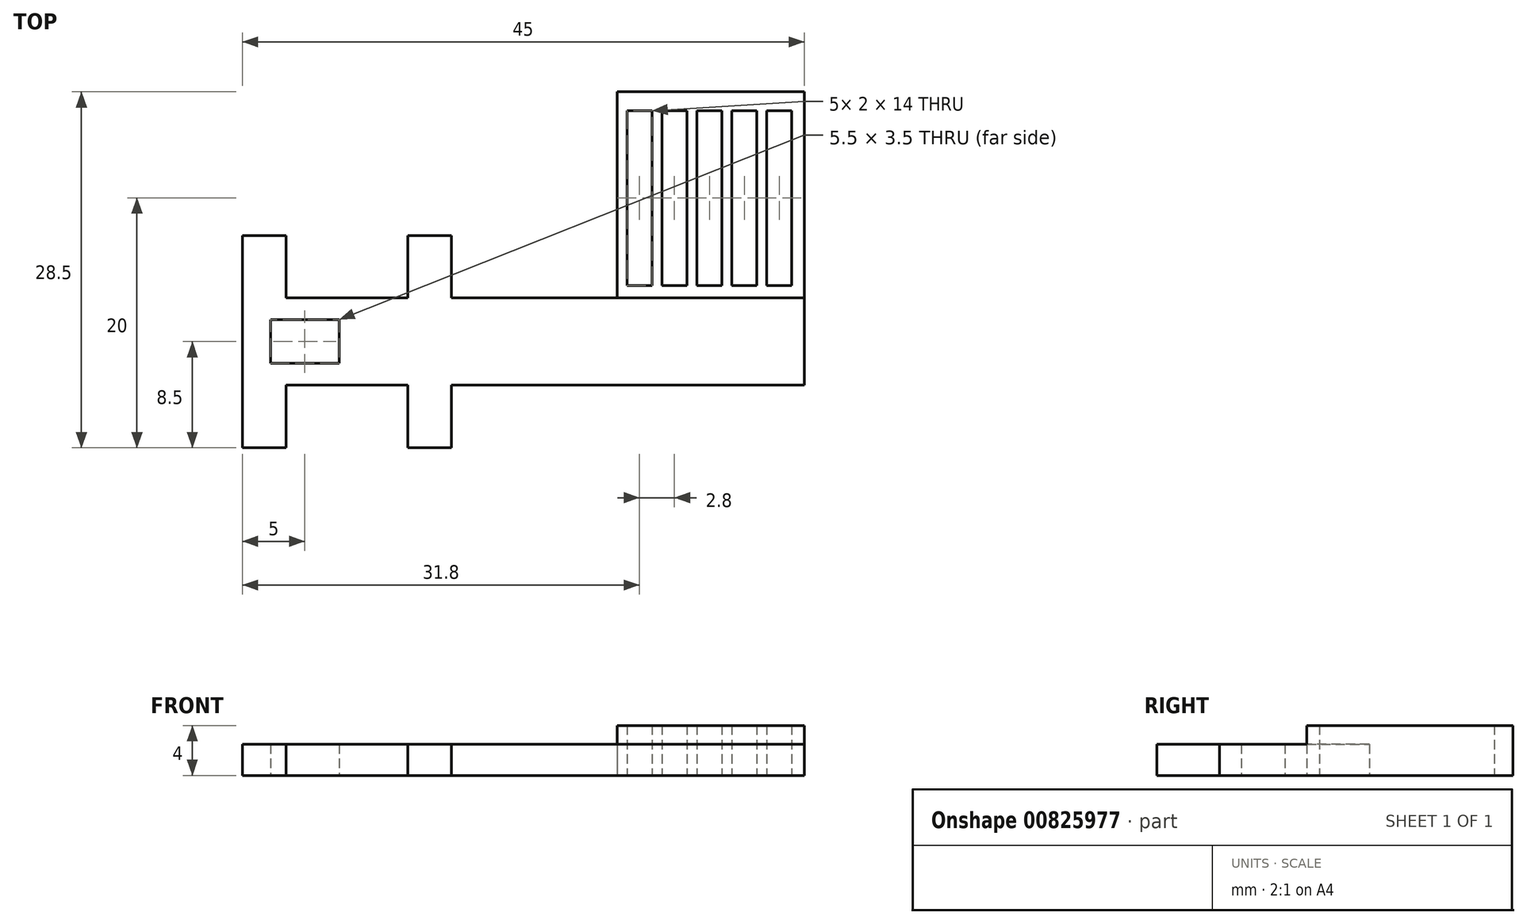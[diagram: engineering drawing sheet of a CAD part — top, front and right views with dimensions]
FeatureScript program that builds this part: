
annotation { "Feature Type Name" : "Feature", "Feature Type Description" : "" }
export const myFeature = defineFeature(function(context is Context, id is Id, definition is map)
    precondition{}
    {
        {
            var Q0;
            Q0=qCreatedBy(makeId("Top.planeOp"),FACE);
            var sketch = newSketch(context, id + "F0", { "sketchPlane" : qUnion([Q0])});
            skLineSegment(sketch, "E0.bottom", {"start": v(15, 3.5) * mm, "end": v(-15, 3.5) * mm});
            skLineSegment(sketch, "E0.top", {"start": v(15, -3.5) * mm, "end": v(-15, -3.5) * mm});
            skLineSegment(sketch, "E0.left", {"start": v(15, 3.5) * mm, "end": v(15, -3.5) * mm});
            skLineSegment(sketch, "E0.right", {"start": v(-15, 3.5) * mm, "end": v(-15, -3.5) * mm});
            skPoint(sketch, "E0.middle", {"position": v(0, 0) * mm});
            skLineSegment(sketch, "E1.bottom", {"start": v(-12.75, 1.75) * mm, "end": v(-7.25, 1.75) * mm});
            skLineSegment(sketch, "E1.top", {"start": v(-12.75, -1.75) * mm, "end": v(-7.25, -1.75) * mm});
            skLineSegment(sketch, "E1.left", {"start": v(-12.75, 1.75) * mm, "end": v(-12.75, -1.75) * mm});
            skLineSegment(sketch, "E1.right", {"start": v(-7.25, 1.75) * mm, "end": v(-7.25, -1.75) * mm});
            skPoint(sketch, "E1.middle", {"position": v(-10, 0) * mm});
            skLineSegment(sketch, "E2.bottom", {"start": v(1.75, 3.5) * mm, "end": v(-1.75, 3.5) * mm});
            skLineSegment(sketch, "E2.top", {"start": v(1.75, 8.5) * mm, "end": v(-1.75, 8.5) * mm});
            skLineSegment(sketch, "E2.left", {"start": v(1.75, 3.5) * mm, "end": v(1.75, 8.5) * mm});
            skLineSegment(sketch, "E2.right", {"start": v(-1.75, 3.5) * mm, "end": v(-1.75, 8.5) * mm});
            skPoint(sketch, "E2.middle", {"position": v(0, 6) * mm});
            skPoint(sketch, "E2.middle.positionSnap0", {"position": v(0, 3.5) * mm});
            skPoint(sketch, "E2.centerSnap0", {"position": v(0, 3.5) * mm});
            skLineSegment(sketch, "E3.bottom", {"start": v(1.75, -3.5) * mm, "end": v(-1.75, -3.5) * mm});
            skLineSegment(sketch, "E3.top", {"start": v(1.75, -8.5) * mm, "end": v(-1.75, -8.5) * mm});
            skLineSegment(sketch, "E3.left", {"start": v(1.75, -3.5) * mm, "end": v(1.75, -8.5) * mm});
            skLineSegment(sketch, "E3.right", {"start": v(-1.75, -3.5) * mm, "end": v(-1.75, -8.5) * mm});
            skPoint(sketch, "E3.middle", {"position": v(0, -6) * mm});
            skLineSegment(sketch, "E4.bottom", {"start": v(-15, 3.5) * mm, "end": v(-11.5, 3.5) * mm});
            skLineSegment(sketch, "E4.top", {"start": v(-15, 8.5) * mm, "end": v(-11.5, 8.5) * mm});
            skLineSegment(sketch, "E4.left", {"start": v(-15, 3.5) * mm, "end": v(-15, 8.5) * mm});
            skLineSegment(sketch, "E4.right", {"start": v(-11.5, 3.5) * mm, "end": v(-11.5, 8.5) * mm});
            skPoint(sketch, "E4.middle", {"position": v(-13.25, 6) * mm});
            skLineSegment(sketch, "E5.bottom", {"start": v(-15, -3.5) * mm, "end": v(-11.5, -3.5) * mm});
            skLineSegment(sketch, "E5.top", {"start": v(-15, -8.5) * mm, "end": v(-11.5, -8.5) * mm});
            skLineSegment(sketch, "E5.left", {"start": v(-15, -3.5) * mm, "end": v(-15, -8.5) * mm});
            skLineSegment(sketch, "E5.right", {"start": v(-11.5, -3.5) * mm, "end": v(-11.5, -8.5) * mm});
            skPoint(sketch, "E5.middle", {"position": v(-13.25, -6) * mm});
            skLineSegment(sketch, "E6.bottom", {"start": v(15, 3.5) * mm, "end": v(15, 3.5) * mm});
            skLineSegment(sketch, "E6.top", {"start": v(15, -3.5) * mm, "end": v(15, -3.5) * mm});
            skLineSegment(sketch, "E7.bottom", {"start": v(15, 3.5) * mm, "end": v(30, 3.5) * mm});
            skLineSegment(sketch, "E7.top", {"start": v(15, -3.5) * mm, "end": v(30, -3.5) * mm});
            skLineSegment(sketch, "E7.right", {"start": v(30, 3.5) * mm, "end": v(30, -3.5) * mm});
            skLineSegment(sketch, "E8.top", {"start": v(15, 20) * mm, "end": v(30, 20) * mm});
            skLineSegment(sketch, "E8.left", {"start": v(15, 3.5) * mm, "end": v(15, 20) * mm});
            skLineSegment(sketch, "E8.right", {"start": v(30, 3.5) * mm, "end": v(30, 20) * mm});
            skLineSegment(sketch, "E9.bottom", {"start": v(15.8, 18.5) * mm, "end": v(17.8, 18.5) * mm});
            skLineSegment(sketch, "E9.top", {"start": v(15.8, 4.5) * mm, "end": v(17.8, 4.5) * mm});
            skLineSegment(sketch, "E9.left", {"start": v(15.8, 18.5) * mm, "end": v(15.8, 4.5) * mm});
            skLineSegment(sketch, "E9.right", {"start": v(17.8, 18.5) * mm, "end": v(17.8, 4.5) * mm});
            skLineSegment(sketch, "E10.bottom", {"start": v(18.6, 18.5) * mm, "end": v(20.6, 18.5) * mm});
            skLineSegment(sketch, "E10.top", {"start": v(18.6, 4.5) * mm, "end": v(20.6, 4.5) * mm});
            skLineSegment(sketch, "E10.left", {"start": v(18.6, 18.5) * mm, "end": v(18.6, 4.5) * mm});
            skLineSegment(sketch, "E10.right", {"start": v(20.6, 18.5) * mm, "end": v(20.6, 4.5) * mm});
            skLineSegment(sketch, "E11.bottom", {"start": v(21.4, 18.5) * mm, "end": v(23.4, 18.5) * mm});
            skLineSegment(sketch, "E11.top", {"start": v(21.4, 4.5) * mm, "end": v(23.4, 4.5) * mm});
            skLineSegment(sketch, "E11.left", {"start": v(21.4, 18.5) * mm, "end": v(21.4, 4.5) * mm});
            skLineSegment(sketch, "E11.right", {"start": v(23.4, 18.5) * mm, "end": v(23.4, 4.5) * mm});
            skLineSegment(sketch, "E12.bottom", {"start": v(24.2, 18.5) * mm, "end": v(26.2, 18.5) * mm});
            skLineSegment(sketch, "E12.top", {"start": v(24.2, 4.5) * mm, "end": v(26.2, 4.5) * mm});
            skLineSegment(sketch, "E12.left", {"start": v(24.2, 18.5) * mm, "end": v(24.2, 4.5) * mm});
            skLineSegment(sketch, "E12.right", {"start": v(26.2, 18.5) * mm, "end": v(26.2, 4.5) * mm});
            skLineSegment(sketch, "E13.bottom", {"start": v(27, 18.5) * mm, "end": v(29, 18.5) * mm});
            skLineSegment(sketch, "E13.top", {"start": v(27, 4.5) * mm, "end": v(29, 4.5) * mm});
            skLineSegment(sketch, "E13.left", {"start": v(27, 18.5) * mm, "end": v(27, 4.5) * mm});
            skLineSegment(sketch, "E13.right", {"start": v(29, 18.5) * mm, "end": v(29, 4.5) * mm});
            skSolve(sketch);
        }
        {
            var Q0;
            Q0=makeQuery(id+"F0.imprint","IMPRINT",FACE,{"disambiguationData":[TD([[makeQuery(id+"F0.imprint","IMPRINT",EDGE,{"derivedFrom":sQuery(id+"F0.wireOp",EDGE,"E2.top")}),1.0]])]});
            var Q1;
            {var subQ1=sQuery(id+"F0.wireOp",EDGE,"E0.left");Q1=makeQuery(id+"F0.imprint","IMPRINT",FACE,{"disambiguationData":[TD([[makeQuery(id+"F0.imprint","IMPRINT",EDGE,{"derivedFrom":subQ1}),-1.0]])]});}
            var Q2;
            Q2=makeQuery(id+"F0.imprint","IMPRINT",FACE,{"disambiguationData":[TD([[makeQuery(id+"F0.imprint","IMPRINT",EDGE,{"derivedFrom":sQuery(id+"F0.wireOp",EDGE,"E3.top")}),-1.0]])]});
            var Q3;
            Q3=makeQuery(id+"F0.imprint","IMPRINT",FACE,{"disambiguationData":[TD([[makeQuery(id+"F0.imprint","IMPRINT",EDGE,{"derivedFrom":sQuery(id+"F0.wireOp",EDGE,"E4.top")}),-1.0]])]});
            var Q4;
            Q4=makeQuery(id+"F0.imprint","IMPRINT",FACE,{"disambiguationData":[TD([[makeQuery(id+"F0.imprint","IMPRINT",EDGE,{"derivedFrom":sQuery(id+"F0.wireOp",EDGE,"E5.top")}),1.0]])]});
            var Q5;
            {var subQ1=sQuery(id+"F0.wireOp",EDGE,"E0.left");Q5=makeQuery(id+"F0.imprint","IMPRINT",FACE,{"disambiguationData":[TD([[makeQuery(id+"F0.imprint","IMPRINT",EDGE,{"derivedFrom":subQ1}),-1.0]])]});}
            var Q6;
            Q6=makeQuery(id+"F0.imprint","IMPRINT",FACE,{"disambiguationData":[TD([[makeQuery(id+"F0.imprint","IMPRINT",EDGE,{"derivedFrom":sQuery(id+"F0.wireOp",EDGE,"E7.bottom")}),-1.0]])]});
            var Q7;
            Q7=makeQuery(id+"F0.imprint","IMPRINT",FACE,{"disambiguationData":[TD([[makeQuery(id+"F0.imprint","IMPRINT",EDGE,{"derivedFrom":sQuery(id+"F0.wireOp",EDGE,"E0.left")}),1.0]])]});
            extrude(context, id + "F1", {"entities" : qUnion([Q0, Q1, Q2, Q3, Q4, Q5, Q6, Q7]), "depth" : 2.5 * mm, "offsetDistance" : 25 * mm});
        }
        {
            var Q0;
            Q0=makeQuery(id+"F0.imprint","IMPRINT",FACE,{"disambiguationData":[TD([[makeQuery(id+"F0.imprint","IMPRINT",EDGE,{"derivedFrom":sQuery(id+"F0.wireOp",EDGE,"E7.bottom")}),1.0]])]});
            extrude(context, id + "F2", {"entities" : qUnion([Q0]), "operationType" : NewBodyOperationType.ADD, "depth" : 4 * mm, "offsetDistance" : 25 * mm});
        }
    });
